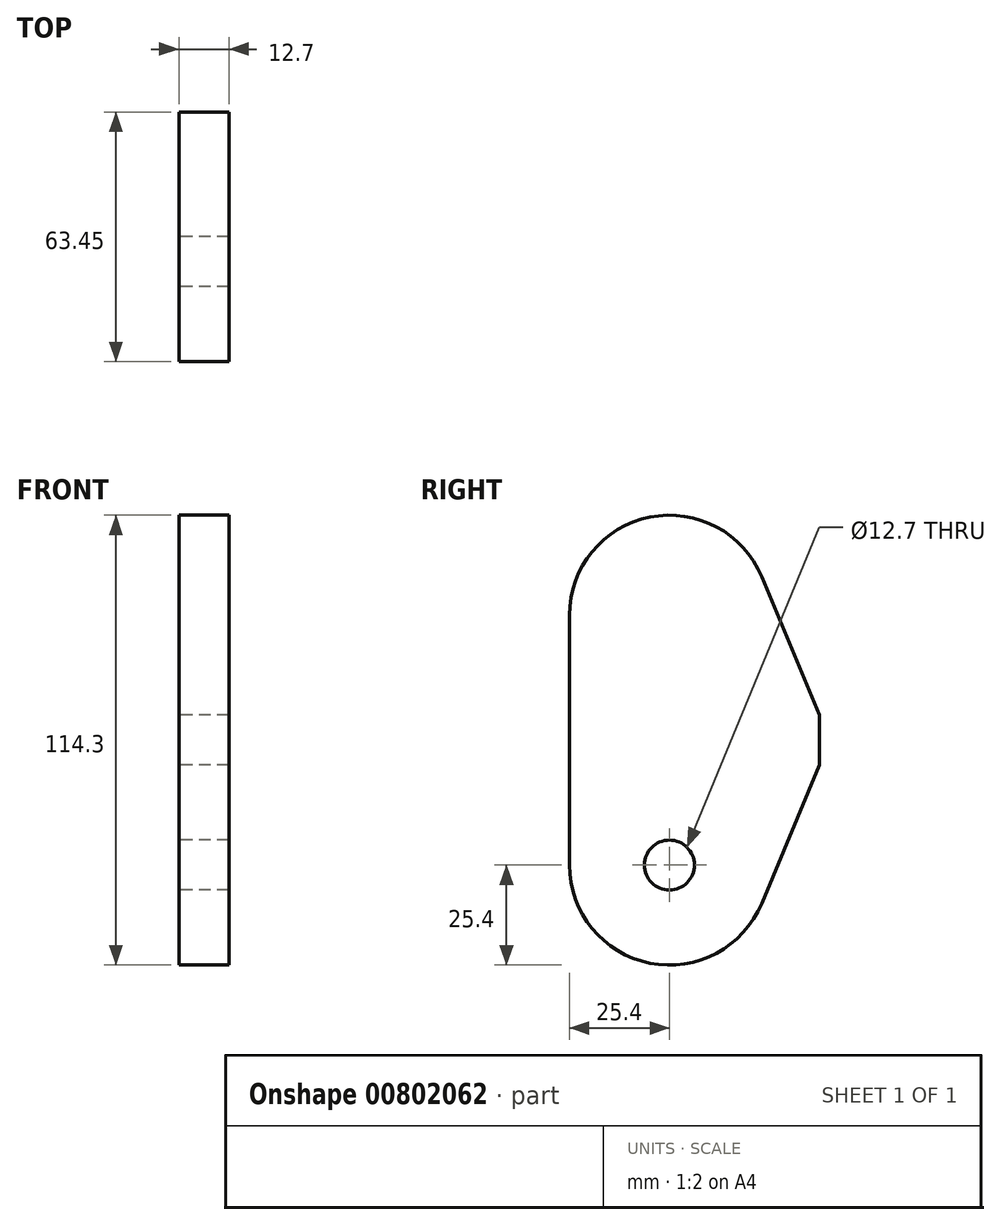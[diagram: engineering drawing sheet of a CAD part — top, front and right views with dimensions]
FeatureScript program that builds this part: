
annotation { "Feature Type Name" : "Feature", "Feature Type Description" : "" }
export const myFeature = defineFeature(function(context is Context, id is Id, definition is map)
    precondition{}
    {
        {
            var Q0;
            Q0=qCreatedBy(makeId("Right.planeOp"),FACE);
            var sketch = newSketch(context, id + "F0", { "sketchPlane" : qUnion([Q0])});
            skCircle(sketch, "E0", {"center": v(0, 0) * mm, "radius": 6.35 * mm});
            skLineSegment(sketch, "E1", {"start": v(0, 0) * mm, "end": v(0, 63.5) * mm, "construction": true});
            skArc(sketch, "E2", {"start": v(23.46, -9.74) * mm, "mid": v(-4.97, -24.9) * mm, "end": v(-25.4, 0) * mm});
            skArc(sketch, "E3", {"start": v(-25.4, 63.5) * mm, "mid": v(-4.97, 88.4) * mm, "end": v(23.46, 73.24) * mm});
            skLineSegment(sketch, "E4", {"start": v(-25.4, 63.5) * mm, "end": v(-25.4, 0) * mm});
            skLineSegment(sketch, "E5", {"start": v(38.05, 38.1) * mm, "end": v(38.05, 25.4) * mm});
            skLineSegment(sketch, "E6", {"start": v(0, 31.75) * mm, "end": v(40.93, 31.75) * mm, "construction": true});
            skPoint(sketch, "E6.endSnap0", {"position": v(0, 31.75) * mm});
            skLineSegment(sketch, "E7", {"start": v(38.05, 38.1) * mm, "end": v(23.46, 73.24) * mm});
            skLineSegment(sketch, "E8", {"start": v(38.05, 25.4) * mm, "end": v(23.46, -9.74) * mm});
            skSolve(sketch);
        }
        {
            var Q0;
            Q0=qSketchRegion(id+"F0",true);
            extrude(context, id + "F1", {"entities" : qUnion([Q0]), "depth" : 12.7 * mm});
        }
    });
